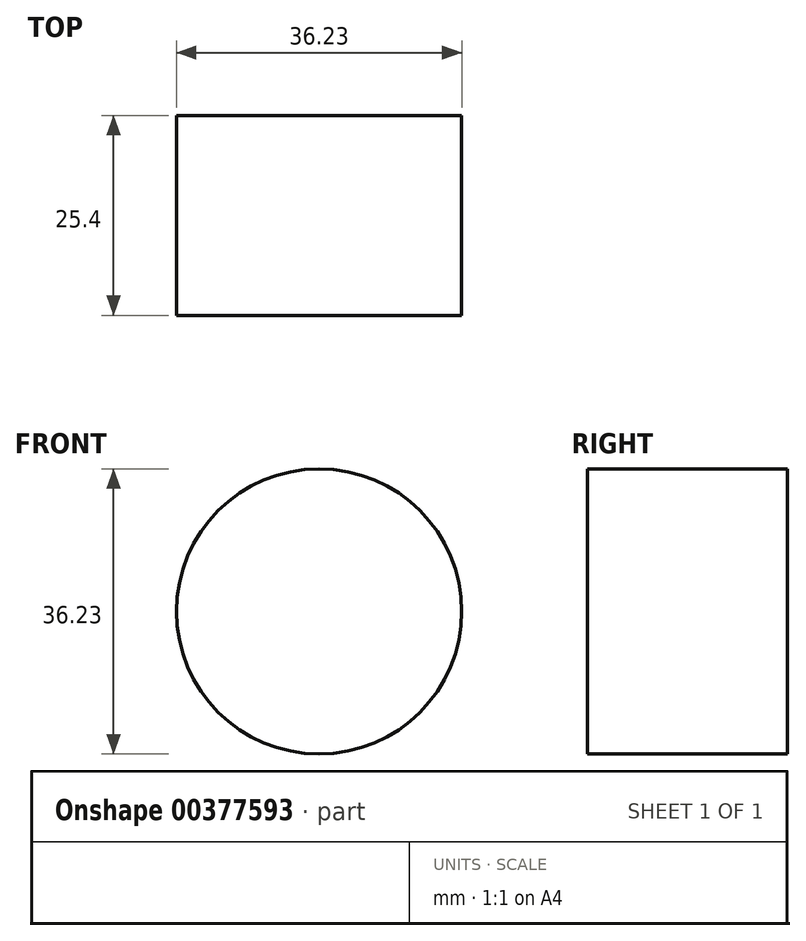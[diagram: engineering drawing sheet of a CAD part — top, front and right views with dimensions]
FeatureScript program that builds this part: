
annotation { "Feature Type Name" : "Feature", "Feature Type Description" : "" }
export const myFeature = defineFeature(function(context is Context, id is Id, definition is map)
    precondition{}
    {
        {
            var Q0;
            Q0=qCreatedBy(makeId("Front.planeOp"),FACE);
            var sketch = newSketch(context, id + "F0", { "sketchPlane" : qUnion([Q0])});
            skCircle(sketch, "E0", {"center": v(-10.84, 7.49) * mm, "radius": 18.12 * mm});
            skSolve(sketch);
        }
        {
            var Q0;
            Q0 = qSketchRegion(id + "F0", true);
            extrude(context, id + "F1", {"entities" : qUnion([Q0]), "depth" : 25.4 * mm});
        }
    });
